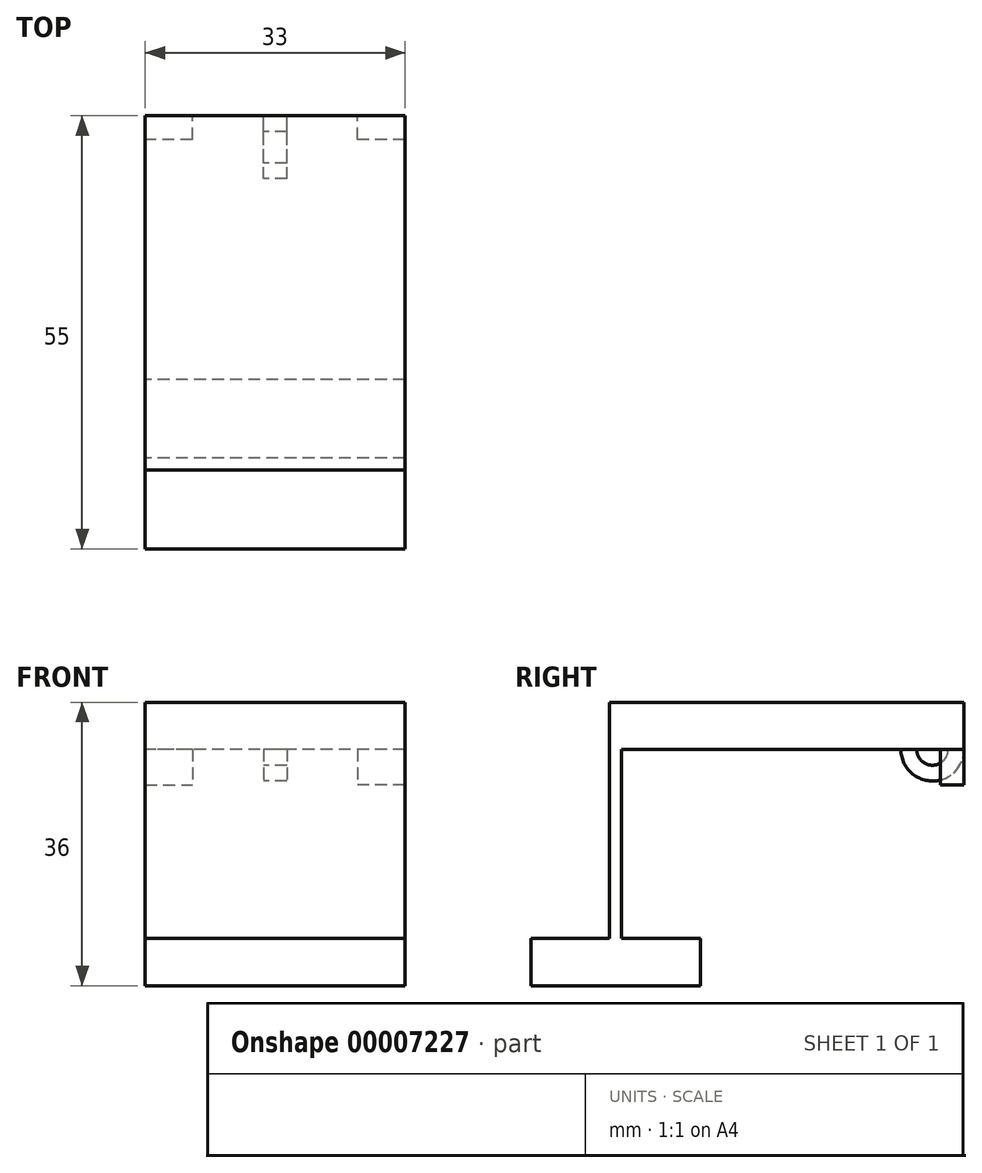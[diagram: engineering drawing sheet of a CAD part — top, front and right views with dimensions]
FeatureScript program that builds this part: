
annotation { "Feature Type Name" : "Feature", "Feature Type Description" : "" }
export const myFeature = defineFeature(function(context is Context, id is Id, definition is map)
    precondition{}
    {
        {
            var Q0;
            Q0=qCreatedBy(makeId("Right.planeOp"),FACE);
            var sketch = newSketch(context, id + "F0", { "sketchPlane" : qUnion([Q0])});
            skLineSegment(sketch, "E0", {"start": v(1.5, 30) * mm, "end": v(42, 30) * mm});
            skLineSegment(sketch, "E1", {"start": v(45, 30) * mm, "end": v(45, 36) * mm});
            skLineSegment(sketch, "E2", {"start": v(45, 36) * mm, "end": v(0, 36) * mm});
            skLineSegment(sketch, "E3", {"start": v(0, 36) * mm, "end": v(0, 6) * mm});
            skLineSegment(sketch, "E4", {"start": v(0, 0) * mm, "end": v(11.5, 0) * mm});
            skLineSegment(sketch, "E5", {"start": v(1.5, 30) * mm, "end": v(1.5, 6) * mm});
            skLineSegment(sketch, "E6", {"start": v(1.5, 6) * mm, "end": v(11.5, 6) * mm});
            skLineSegment(sketch, "E7", {"start": v(11.5, 6) * mm, "end": v(11.5, 0) * mm});
            skPoint(sketch, "E8", {"position": v(42, 30) * mm});
            skPoint(sketch, "E9", {"position": v(0, 30) * mm});
            skPoint(sketch, "E10", {"position": v(0, 6) * mm});
            skLineSegment(sketch, "E11", {"start": v(0, 6) * mm, "end": v(-10, 6) * mm});
            skLineSegment(sketch, "E12", {"start": v(-10, 6) * mm, "end": v(-10, 0) * mm});
            skLineSegment(sketch, "E13", {"start": v(-10, 0) * mm, "end": v(0, 0) * mm});
            skPoint(sketch, "E14.end.orphan", {"position": v(45, 22.38) * mm});
            skLineSegment(sketch, "E15", {"start": v(42, 30) * mm, "end": v(45, 30) * mm});
            skSolve(sketch);
        }
        {
            var Q0;
            Q0=qSketchRegion(id+"F0",true);
            extrude(context, id + "F1", {"entities" : qUnion([Q0]), "depth" : 33 * mm});
        }
        {
            var Q0;
            Q0=makeQuery(id+"F1.opExtrude","CAP_FACE",FACE,{"disambiguationData":[OSD([sQuery(id+"F0.wireOp",EDGE,"E0"),sQuery(id+"F0.wireOp",EDGE,"E1"),sQuery(id+"F0.wireOp",EDGE,"E2"),sQuery(id+"F0.wireOp",EDGE,"E3"),sQuery(id+"F0.wireOp",EDGE,"E4"),sQuery(id+"F0.wireOp",EDGE,"E5"),sQuery(id+"F0.wireOp",EDGE,"E6"),sQuery(id+"F0.wireOp",EDGE,"E7"),sQuery(id+"F0.wireOp",EDGE,"E11"),sQuery(id+"F0.wireOp",EDGE,"E12"),sQuery(id+"F0.wireOp",EDGE,"E13"),sQuery(id+"F0.wireOp",EDGE,"E15")])],"isStart":false});
            var sketch = newSketch(context, id + "F2", { "sketchPlane" : qUnion([Q0])});
            skArc(sketch, "E16", {"start": v(37, 30) * mm, "mid": v(41, 26) * mm, "end": v(45, 30) * mm});
            skArc(sketch, "E17", {"start": v(39, 30) * mm, "mid": v(41, 28) * mm, "end": v(43, 30) * mm});
            skLineSegment(sketch, "E18", {"start": v(39, 30) * mm, "end": v(37, 30) * mm});
            skLineSegment(sketch, "E19", {"start": v(37, 30) * mm, "end": v(39, 30) * mm});
            skLineSegment(sketch, "E20", {"start": v(43, 30) * mm, "end": v(45, 30) * mm});
            skSolve(sketch);
        }
        {
            var Q0;
            Q0=qSketchRegion(id+"F2",true);
            extrude(context, id + "F3", {"entities" : qUnion([Q0]), "depth" : 3 * mm});
        }
        {
            var Q0;
            Q0=makeQuery(id+"F3.opExtrude","SWEPT_BODY",BODY,{"disambiguationData":[OSD([sQuery(id+"F2.wireOp",EDGE,"E16"),sQuery(id+"F2.wireOp",EDGE,"E17"),sQuery(id+"F2.wireOp",EDGE,"E19"),sQuery(id+"F2.wireOp",EDGE,"E20")])]});
            var Q1;
            Q1=makeQuery(id+"F1.opExtrude","SWEPT_EDGE",EDGE,{"disambiguationData":[OSD([sQuery(id+"F0.wireOp",EDGE,"E1"),sQuery(id+"F0.wireOp",EDGE,"E15")])]});
            transform(context, id + "F4", {"entities" : qUnion([Q0]), "transformType" : TransformType.TRANSLATION_DISTANCE, "transformDirection" : qUnion([Q1]), "distance" : 18 * mm, "makeCopy" : false});
        }
        {
            var Q0;
            Q0=makeQuery(id+"F1.opExtrude","SWEPT_FACE",FACE,{"disambiguationData":[OSD([sQuery(id+"F0.wireOp",EDGE,"E1")])]});
            var sketch = newSketch(context, id + "F5", { "sketchPlane" : qUnion([Q0])});
            skLineSegment(sketch, "E21.bottom", {"start": v(-33, 30) * mm, "end": v(-27, 30) * mm});
            skLineSegment(sketch, "E21.top", {"start": v(-33, 25.5) * mm, "end": v(-27, 25.5) * mm});
            skLineSegment(sketch, "E21.left", {"start": v(-33, 30) * mm, "end": v(-33, 25.5) * mm});
            skLineSegment(sketch, "E21.right", {"start": v(-27, 30) * mm, "end": v(-27, 25.5) * mm});
            skLineSegment(sketch, "E22.bottom", {"start": v(0, 30) * mm, "end": v(-6, 30) * mm});
            skLineSegment(sketch, "E22.top", {"start": v(0, 25.5) * mm, "end": v(-6, 25.5) * mm});
            skLineSegment(sketch, "E22.left", {"start": v(0, 30) * mm, "end": v(0, 25.5) * mm});
            skLineSegment(sketch, "E22.right", {"start": v(-6, 30) * mm, "end": v(-6, 25.5) * mm});
            skLineSegment(sketch, "E23", {"start": v(-16.5, 30) * mm, "end": v(-16.5, 12.44) * mm, "construction": true});
            skSolve(sketch);
        }
        {
            var Q0;
            Q0=qSketchRegion(id+"F5",true);
            extrude(context, id + "F6", {"entities" : qUnion([Q0]), "oppositeDirection" : true, "depth" : 3 * mm});
        }
    });
